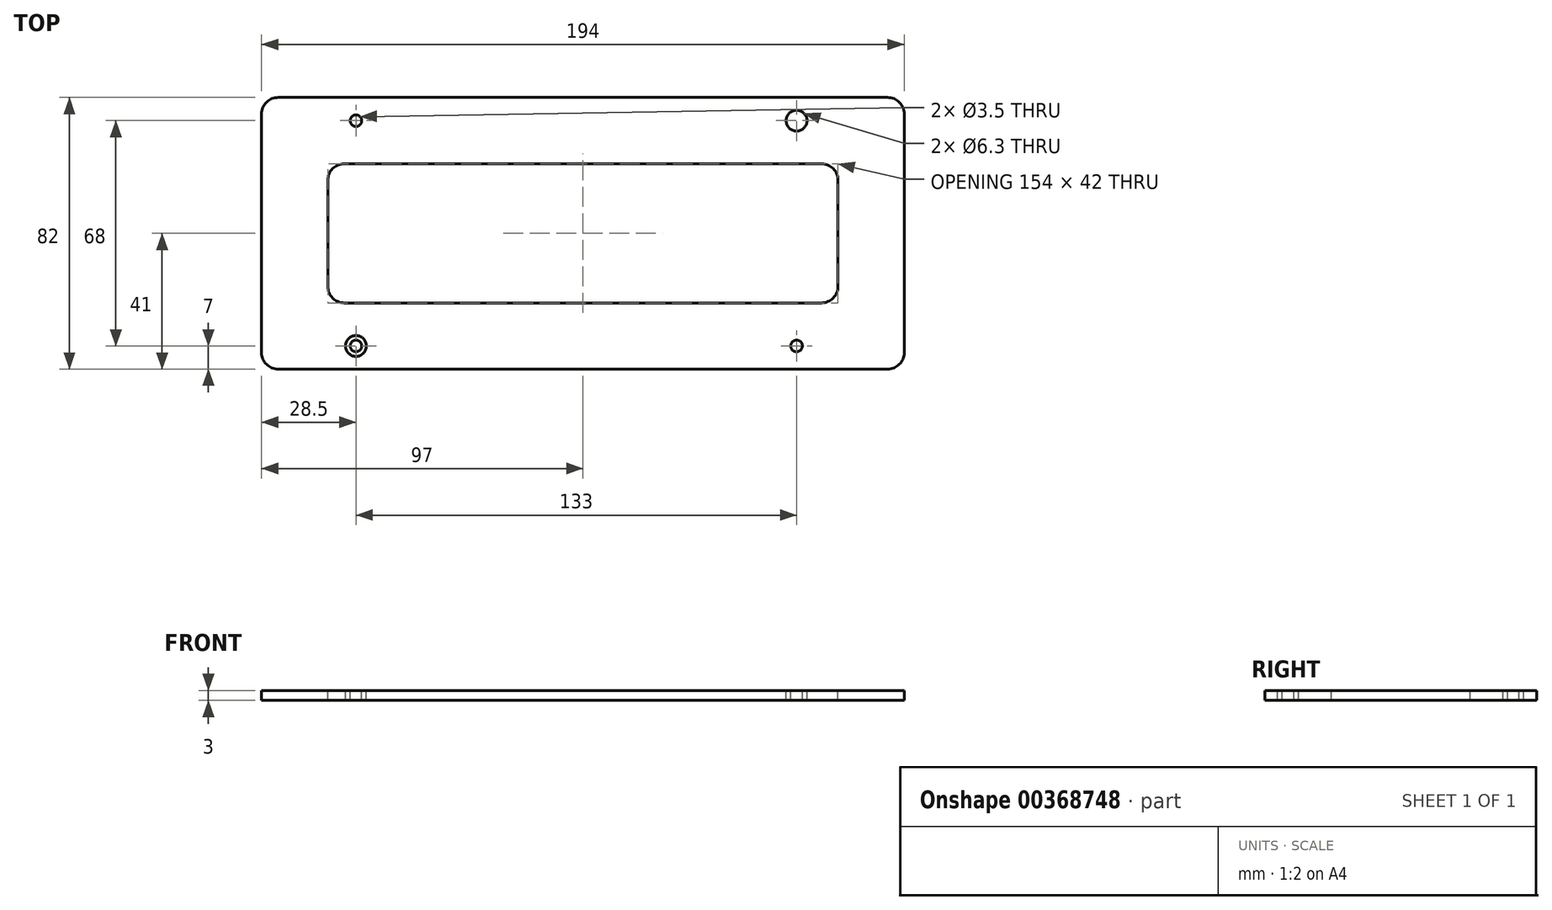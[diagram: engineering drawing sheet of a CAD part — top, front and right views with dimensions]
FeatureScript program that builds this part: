
annotation { "Feature Type Name" : "Feature", "Feature Type Description" : "" }
export const myFeature = defineFeature(function(context is Context, id is Id, definition is map)
    precondition{}
    {
        {
            var Q0;
            Q0=qCreatedBy(makeId("Top.planeOp"),FACE);
            var sketch = newSketch(context, id + "F0", { "sketchPlane" : qUnion([Q0])});
            skLineSegment(sketch, "E0.bottom", {"start": v(-97, 41) * mm, "end": v(97, 41) * mm});
            skLineSegment(sketch, "E0.top", {"start": v(-97, -41) * mm, "end": v(97, -41) * mm});
            skLineSegment(sketch, "E0.left", {"start": v(-97, 41) * mm, "end": v(-97, -41) * mm});
            skLineSegment(sketch, "E0.right", {"start": v(97, 41) * mm, "end": v(97, -41) * mm});
            skPoint(sketch, "E0.middle", {"position": v(0, 0) * mm});
            skCircle(sketch, "E1", {"center": v(-68.5, 34) * mm, "radius": 1.75 * mm});
            skCircle(sketch, "E2.MirrorC", {"center": v(-68.5, -34) * mm, "radius": 1.75 * mm});
            skLineSegment(sketch, "E3.bottom", {"start": v(-77, 21) * mm, "end": v(77, 21) * mm});
            skLineSegment(sketch, "E3.top", {"start": v(-77, -21) * mm, "end": v(77, -21) * mm});
            skLineSegment(sketch, "E3.left", {"start": v(-77, 21) * mm, "end": v(-77, -21) * mm});
            skLineSegment(sketch, "E3.right", {"start": v(77, 21) * mm, "end": v(77, -21) * mm});
            skCircle(sketch, "E4", {"center": v(-68.5, 34) * mm, "radius": 3.15 * mm});
            skCircle(sketch, "E5.MirrorC", {"center": v(-68.5, -34) * mm, "radius": 3.15 * mm});
            skLineSegment(sketch, "E6", {"start": v(-2, 49.04) * mm, "end": v(-2, -43.84) * mm, "construction": true});
            skCircle(sketch, "E7.MirrorC", {"center": v(64.5, 34) * mm, "radius": 3.15 * mm});
            skCircle(sketch, "E8.MirrorC", {"center": v(64.5, 34) * mm, "radius": 1.75 * mm});
            skCircle(sketch, "E9.MirrorC", {"center": v(64.5, -34) * mm, "radius": 3.15 * mm});
            skCircle(sketch, "E10.MirrorC", {"center": v(64.5, -34) * mm, "radius": 1.75 * mm});
            skSolve(sketch);
        }
        {
            var Q0;
            Q0=makeQuery(id+"F0.imprint","IMPRINT",FACE,{"disambiguationData":[TD([[makeQuery(id+"F0.imprint","IMPRINT",EDGE,{"derivedFrom":sQuery(id+"F0.wireOp",EDGE,"E0.bottom")}),-1.0]])]});
            var Q1;
            Q1=makeQuery(id+"F0.imprint","IMPRINT",FACE,{"disambiguationData":[TD([[makeQuery(id+"F0.imprint","IMPRINT",EDGE,{"derivedFrom":sQuery(id+"F0.wireOp",EDGE,"E1")}),-1.0]])]});
            var Q2;
            Q2=makeQuery(id+"F0.imprint","IMPRINT",FACE,{"disambiguationData":[TD([[makeQuery(id+"F0.imprint","IMPRINT",EDGE,{"derivedFrom":sQuery(id+"F0.wireOp",EDGE,"158bd95f-0d2a-40ff-bf6f-3f83f863d0ac0.MirrorC")}),1.0]])]});
            var Q3;
            Q3=makeQuery(id+"F0.imprint","IMPRINT",FACE,{"disambiguationData":[TD([[makeQuery(id+"F0.imprint","IMPRINT",EDGE,{"derivedFrom":sQuery(id+"F0.wireOp",EDGE,"3c385fd1-c402-4ea0-89ec-4e35221334e60.MirrorC")}),-1.0]])]});
            var Q4;
            Q4=makeQuery(id+"F0.imprint","IMPRINT",FACE,{"disambiguationData":[TD([[makeQuery(id+"F0.imprint","IMPRINT",EDGE,{"derivedFrom":sQuery(id+"F0.wireOp",EDGE,"E2.MirrorC")}),1.0]])]});
            var Q5;
            Q5=makeQuery(id+"F0.imprint","IMPRINT",FACE,{"disambiguationData":[TD([[makeQuery(id+"F0.imprint","IMPRINT",EDGE,{"derivedFrom":sQuery(id+"F0.wireOp",EDGE,"E7.MirrorC")}),-1.0]])]});
            var Q6;
            Q6=makeQuery(id+"F0.imprint","IMPRINT",FACE,{"disambiguationData":[TD([[makeQuery(id+"F0.imprint","IMPRINT",EDGE,{"derivedFrom":sQuery(id+"F0.wireOp",EDGE,"E9.MirrorC")}),1.0]])]});
            extrude(context, id + "F1", {"entities" : qUnion([Q0, Q1, Q2, Q3, Q4, Q5, Q6]), "oppositeDirection" : true, "depth" : 9 * mm, "offsetDistance" : 25 * mm});
        }
        {
            var Q0;
            Q0=makeQuery(id+"F0.imprint","IMPRINT",FACE,{"disambiguationData":[TD([[makeQuery(id+"F0.imprint","IMPRINT",EDGE,{"derivedFrom":sQuery(id+"F0.wireOp",EDGE,"E1")}),-1.0]])]});
            var Q1;
            Q1=makeQuery(id+"F0.imprint","IMPRINT",FACE,{"disambiguationData":[TD([[makeQuery(id+"F0.imprint","IMPRINT",EDGE,{"derivedFrom":sQuery(id+"F0.wireOp",EDGE,"158bd95f-0d2a-40ff-bf6f-3f83f863d0ac0.MirrorC")}),1.0]])]});
            var Q2;
            Q2=makeQuery(id+"F0.imprint","IMPRINT",FACE,{"disambiguationData":[TD([[makeQuery(id+"F0.imprint","IMPRINT",EDGE,{"derivedFrom":sQuery(id+"F0.wireOp",EDGE,"3c385fd1-c402-4ea0-89ec-4e35221334e60.MirrorC")}),-1.0]])]});
            var Q3;
            Q3=makeQuery(id+"F0.imprint","IMPRINT",FACE,{"disambiguationData":[TD([[makeQuery(id+"F0.imprint","IMPRINT",EDGE,{"derivedFrom":sQuery(id+"F0.wireOp",EDGE,"E2.MirrorC")}),1.0]])]});
            var Q4;
            Q4=makeQuery(id+"F0.imprint","IMPRINT",FACE,{"disambiguationData":[TD([[makeQuery(id+"F0.imprint","IMPRINT",EDGE,{"derivedFrom":sQuery(id+"F0.wireOp",EDGE,"E7.MirrorC")}),-1.0]])]});
            var Q5;
            Q5=makeQuery(id+"F0.imprint","IMPRINT",FACE,{"disambiguationData":[TD([[makeQuery(id+"F0.imprint","IMPRINT",EDGE,{"derivedFrom":sQuery(id+"F0.wireOp",EDGE,"E9.MirrorC")}),1.0]])]});
            extrude(context, id + "F2", {"entities" : qUnion([Q0, Q1, Q2, Q3, Q4, Q5]), "operationType" : NewBodyOperationType.REMOVE, "oppositeDirection" : true, "depth" : 6 * mm, "offsetDistance" : 25 * mm});
        }
        {
            var Q0;
            Q0=makeQuery(id+"F1.opExtrude","SWEPT_EDGE",EDGE,{"disambiguationData":[OSD([sQuery(id+"F0.wireOp",EDGE,"E0.bottom"),sQuery(id+"F0.wireOp",EDGE,"E0.right")])]});
            var Q1;
            Q1=makeQuery(id+"F1.opExtrude","SWEPT_EDGE",EDGE,{"disambiguationData":[OSD([sQuery(id+"F0.wireOp",EDGE,"E0.bottom"),sQuery(id+"F0.wireOp",EDGE,"E0.left")])]});
            var Q2;
            Q2=makeQuery(id+"F1.opExtrude","SWEPT_EDGE",EDGE,{"disambiguationData":[OSD([sQuery(id+"F0.wireOp",EDGE,"E0.top"),sQuery(id+"F0.wireOp",EDGE,"E0.left")])]});
            var Q3;
            Q3=makeQuery(id+"F1.opExtrude","SWEPT_EDGE",EDGE,{"disambiguationData":[OSD([sQuery(id+"F0.wireOp",EDGE,"E0.top"),sQuery(id+"F0.wireOp",EDGE,"E0.right")])]});
            var Q4;
            Q4=makeQuery(id+"F1.opExtrude","SWEPT_EDGE",EDGE,{"disambiguationData":[OSD([sQuery(id+"F0.wireOp",EDGE,"E3.bottom"),sQuery(id+"F0.wireOp",EDGE,"E3.left")])]});
            var Q5;
            Q5=makeQuery(id+"F1.opExtrude","SWEPT_EDGE",EDGE,{"disambiguationData":[OSD([sQuery(id+"F0.wireOp",EDGE,"E3.bottom"),sQuery(id+"F0.wireOp",EDGE,"E3.right")])]});
            var Q6;
            Q6=makeQuery(id+"F1.opExtrude","SWEPT_EDGE",EDGE,{"disambiguationData":[OSD([sQuery(id+"F0.wireOp",EDGE,"E3.top"),sQuery(id+"F0.wireOp",EDGE,"E3.right")])]});
            var Q7;
            Q7=makeQuery(id+"F1.opExtrude","SWEPT_EDGE",EDGE,{"disambiguationData":[OSD([sQuery(id+"F0.wireOp",EDGE,"E3.top"),sQuery(id+"F0.wireOp",EDGE,"E3.left")])]});
            fillet(context, id + "F3", {"entities" : qUnion([Q0, Q1, Q2, Q3, Q4, Q5, Q6, Q7]), "radius" : 5 * mm, "tangentPropagation" : true, "allowEdgeOverflow" : false});
        }
    });
